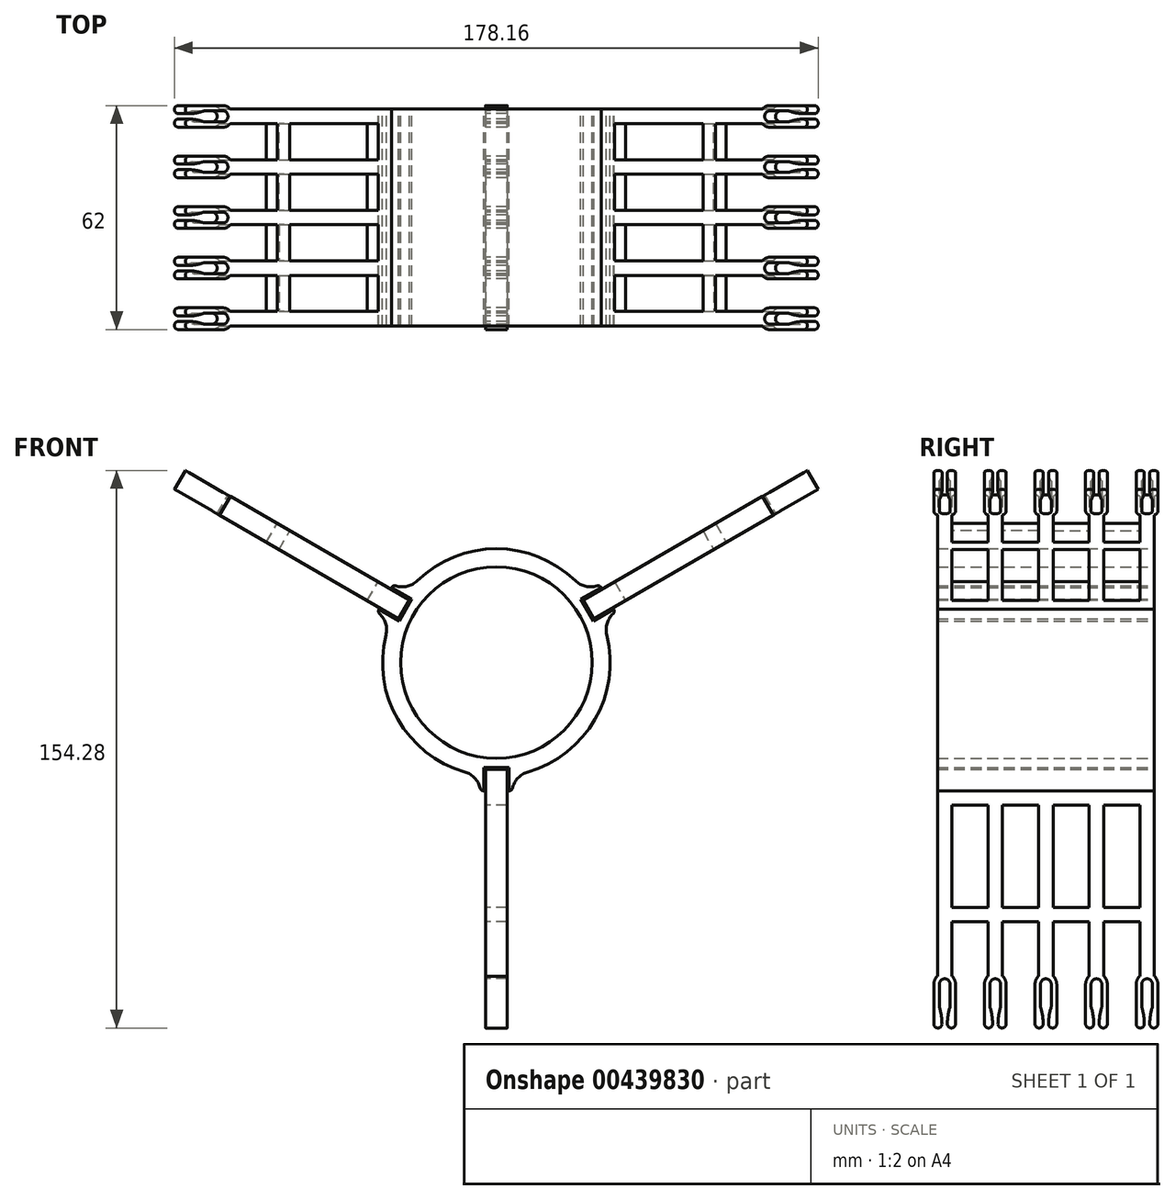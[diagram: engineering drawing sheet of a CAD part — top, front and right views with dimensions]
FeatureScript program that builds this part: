
annotation { "Feature Type Name" : "Feature", "Feature Type Description" : "" }
export const myFeature = defineFeature(function(context is Context, id is Id, definition is map)
    precondition{}
    {
        {
            var Q0;
            Q0=qCreatedBy(makeId("Right.planeOp"),FACE);
            var sketch = newSketch(context, id + "F0", { "sketchPlane" : qUnion([Q0])});
            skLineSegment(sketch, "E0.top", {"start": v(-60, -26.5) * mm, "end": v(0, -26.5) * mm});
            skLineSegment(sketch, "E1.top", {"start": v(-60, -29.5) * mm, "end": v(0, -29.5) * mm});
            skLineSegment(sketch, "E1.left", {"start": v(-60, 0) * mm, "end": v(-60, -29.5) * mm});
            skLineSegment(sketch, "E2", {"start": v(0, -100) * mm, "end": v(0, -29.5) * mm});
            skLineSegment(sketch, "E3", {"start": v(-14, -67.75) * mm, "end": v(-14, -39.5) * mm});
            skLineSegment(sketch, "E4", {"start": v(-14, -39.5) * mm, "end": v(-4, -39.5) * mm});
            skLineSegment(sketch, "E5", {"start": v(-4, -39.5) * mm, "end": v(-4, -67.75) * mm});
            skCircle(sketch, "E6", {"center": v(-4, -39.5) * mm, "radius": 4 * mm, "construction": true});
            skLineSegment(sketch, "E7", {"start": v(-14, -71.75) * mm, "end": v(-4, -71.75) * mm});
            skCircle(sketch, "E8", {"center": v(-4, -71.75) * mm, "radius": 4 * mm, "construction": true});
            skLineSegment(sketch, "E9", {"start": v(0, 0) * mm, "end": v(-60, 0) * mm});
            skLineSegment(sketch, "E10.trimOffspring", {"start": v(0, 0) * mm, "end": v(0, -29.5) * mm});
            skLineSegment(sketch, "E11", {"start": v(0, -32.5) * mm, "end": v(-60, -32.5) * mm, "construction": true});
            skLineSegment(sketch, "E12", {"start": v(0, -35.5) * mm, "end": v(-60, -35.5) * mm, "construction": true});
            skLineSegment(sketch, "E13", {"start": v(-18, -39.5) * mm, "end": v(-28, -39.5) * mm});
            skLineSegment(sketch, "E14", {"start": v(-28, -39.5) * mm, "end": v(-28, -67.75) * mm});
            skLineSegment(sketch, "E15", {"start": v(-18, -71.75) * mm, "end": v(-28, -71.75) * mm});
            skLineSegment(sketch, "E16.trimOffspring", {"start": v(-18, -39.5) * mm, "end": v(-18, -67.75) * mm});
            skLineSegment(sketch, "E17", {"start": v(-28, -67.75) * mm, "end": v(-18, -67.75) * mm});
            skLineSegment(sketch, "E18.MirrorCS", {"start": v(-46, -39.5) * mm, "end": v(-56, -39.5) * mm});
            skLineSegment(sketch, "E19.MirrorCS", {"start": v(-42, -39.5) * mm, "end": v(-42, -67.75) * mm});
            skLineSegment(sketch, "E20.MirrorCS", {"start": v(-46, -67.75) * mm, "end": v(-46, -39.5) * mm});
            skLineSegment(sketch, "E21.MirrorCS", {"start": v(-32, -39.5) * mm, "end": v(-32, -67.75) * mm});
            skLineSegment(sketch, "E22.MirrorCS", {"start": v(-58, -100) * mm, "end": v(-58, -29.5) * mm, "construction": true});
            skLineSegment(sketch, "E23.MirrorCS", {"start": v(-46, -71.75) * mm, "end": v(-56, -71.75) * mm});
            skLineSegment(sketch, "E24.MirrorCS", {"start": v(-56, -71.75) * mm, "end": v(-56, -86.76) * mm});
            skLineSegment(sketch, "E25.MirrorCS", {"start": v(-32, -67.75) * mm, "end": v(-42, -67.75) * mm});
            skLineSegment(sketch, "E26.MirrorCS", {"start": v(-42, -71.75) * mm, "end": v(-32, -71.75) * mm});
            skLineSegment(sketch, "E27.MirrorCS", {"start": v(-56, -39.5) * mm, "end": v(-56, -67.75) * mm});
            skLineSegment(sketch, "E28.MirrorCS", {"start": v(-42, -39.5) * mm, "end": v(-32, -39.5) * mm});
            skLineSegment(sketch, "E29.trimOffspring", {"start": v(-46, -67.75) * mm, "end": v(-56, -67.75) * mm});
            skLineSegment(sketch, "E30.trimOffspring", {"start": v(-14, -67.75) * mm, "end": v(-4, -67.75) * mm});
            skArc(sketch, "E31", {"start": v(-59.5, -95) * mm, "mid": v(-59.48, -95.22) * mm, "end": v(-59.43, -95.44) * mm});
            skArc(sketch, "E32", {"start": v(-56.5, -89) * mm, "mid": v(-58, -87.5) * mm, "end": v(-59.5, -89) * mm});
            skLineSegment(sketch, "E33", {"start": v(-59.5, -89) * mm, "end": v(-59.5, -95) * mm});
            skLineSegment(sketch, "E34", {"start": v(-56.5, -95) * mm, "end": v(-56.5, -89) * mm});
            skArc(sketch, "E35", {"start": v(-56.57, -95.44) * mm, "mid": v(-57.08, -97.7) * mm, "end": v(-57.25, -100) * mm});
            skArc(sketch, "E36", {"start": v(-58.75, -100) * mm, "mid": v(-58.92, -97.7) * mm, "end": v(-59.43, -95.44) * mm});
            skLineSegment(sketch, "E37", {"start": v(-61, -89) * mm, "end": v(-61, -100) * mm});
            skLineSegment(sketch, "E38", {"start": v(-55, -89) * mm, "end": v(-55, -100) * mm});
            skLineSegment(sketch, "E39.trimOffspring", {"start": v(-60, -86.76) * mm, "end": v(-60, -29.5) * mm});
            skArc(sketch, "E40.trimOffspring", {"start": v(-55, -89) * mm, "mid": v(-55.26, -87.78) * mm, "end": v(-56, -86.76) * mm});
            skArc(sketch, "E41.trimOffspring", {"start": v(-56.57, -95.44) * mm, "mid": v(-56.52, -95.22) * mm, "end": v(-56.5, -95) * mm});
            skArc(sketch, "E42.trimOffspring", {"start": v(-60, -86.76) * mm, "mid": v(-60.74, -87.78) * mm, "end": v(-61, -89) * mm});
            skArc(sketch, "E43", {"start": v(-61, -100) * mm, "mid": v(-59.87, -101.12) * mm, "end": v(-58.75, -100) * mm});
            skArc(sketch, "E44", {"start": v(-57.25, -100) * mm, "mid": v(-56.12, -101.12) * mm, "end": v(-55, -100) * mm});
            skArc(sketch, "E45.1.0.0", {"start": v(-46, -86.76) * mm, "mid": v(-46.74, -87.78) * mm, "end": v(-47, -89) * mm});
            skLineSegment(sketch, "E45.1.0.1", {"start": v(-47, -89) * mm, "end": v(-47, -100) * mm});
            skArc(sketch, "E45.1.0.2", {"start": v(-47, -100) * mm, "mid": v(-45.87, -101.12) * mm, "end": v(-44.75, -100) * mm});
            skArc(sketch, "E45.1.0.3", {"start": v(-44.75, -100) * mm, "mid": v(-44.92, -97.7) * mm, "end": v(-45.43, -95.44) * mm});
            skArc(sketch, "E45.1.0.4", {"start": v(-45.5, -95) * mm, "mid": v(-45.48, -95.22) * mm, "end": v(-45.43, -95.44) * mm});
            skLineSegment(sketch, "E45.1.0.5", {"start": v(-45.5, -89) * mm, "end": v(-45.5, -95) * mm});
            skArc(sketch, "E45.1.0.6", {"start": v(-42.5, -89) * mm, "mid": v(-44, -87.5) * mm, "end": v(-45.5, -89) * mm});
            skLineSegment(sketch, "E45.1.0.7", {"start": v(-42.5, -95) * mm, "end": v(-42.5, -89) * mm});
            skArc(sketch, "E45.1.0.8", {"start": v(-42.57, -95.44) * mm, "mid": v(-42.52, -95.22) * mm, "end": v(-42.5, -95) * mm});
            skArc(sketch, "E45.1.0.9", {"start": v(-42.57, -95.44) * mm, "mid": v(-43.08, -97.7) * mm, "end": v(-43.25, -100) * mm});
            skLineSegment(sketch, "E45.1.0.10", {"start": v(-41, -89) * mm, "end": v(-41, -100) * mm});
            skArc(sketch, "E45.1.0.11", {"start": v(-41, -89) * mm, "mid": v(-41.26, -87.78) * mm, "end": v(-42, -86.76) * mm});
            skArc(sketch, "E45.1.0.12", {"start": v(-43.25, -100) * mm, "mid": v(-42.12, -101.12) * mm, "end": v(-41, -100) * mm});
            skArc(sketch, "E45.2.0.0", {"start": v(-32, -86.76) * mm, "mid": v(-32.74, -87.78) * mm, "end": v(-33, -89) * mm});
            skLineSegment(sketch, "E45.2.0.1", {"start": v(-33, -89) * mm, "end": v(-33, -100) * mm});
            skArc(sketch, "E45.2.0.2", {"start": v(-33, -100) * mm, "mid": v(-31.87, -101.12) * mm, "end": v(-30.75, -100) * mm});
            skArc(sketch, "E45.2.0.3", {"start": v(-30.75, -100) * mm, "mid": v(-30.92, -97.7) * mm, "end": v(-31.43, -95.44) * mm});
            skArc(sketch, "E45.2.0.4", {"start": v(-31.5, -95) * mm, "mid": v(-31.48, -95.22) * mm, "end": v(-31.43, -95.44) * mm});
            skLineSegment(sketch, "E45.2.0.5", {"start": v(-31.5, -89) * mm, "end": v(-31.5, -95) * mm});
            skArc(sketch, "E45.2.0.6", {"start": v(-28.5, -89) * mm, "mid": v(-30, -87.5) * mm, "end": v(-31.5, -89) * mm});
            skLineSegment(sketch, "E45.2.0.7", {"start": v(-28.5, -95) * mm, "end": v(-28.5, -89) * mm});
            skArc(sketch, "E45.2.0.8", {"start": v(-28.57, -95.44) * mm, "mid": v(-28.52, -95.22) * mm, "end": v(-28.5, -95) * mm});
            skArc(sketch, "E45.2.0.9", {"start": v(-28.57, -95.44) * mm, "mid": v(-29.08, -97.7) * mm, "end": v(-29.25, -100) * mm});
            skLineSegment(sketch, "E45.2.0.10", {"start": v(-27, -89) * mm, "end": v(-27, -100) * mm});
            skArc(sketch, "E45.2.0.11", {"start": v(-27, -89) * mm, "mid": v(-27.26, -87.78) * mm, "end": v(-28, -86.76) * mm});
            skArc(sketch, "E45.2.0.12", {"start": v(-29.25, -100) * mm, "mid": v(-28.12, -101.12) * mm, "end": v(-27, -100) * mm});
            skArc(sketch, "E45.3.0.0", {"start": v(-18, -86.76) * mm, "mid": v(-18.74, -87.78) * mm, "end": v(-19, -89) * mm});
            skLineSegment(sketch, "E45.3.0.1", {"start": v(-19, -89) * mm, "end": v(-19, -100) * mm});
            skArc(sketch, "E45.3.0.2", {"start": v(-19, -100) * mm, "mid": v(-17.87, -101.12) * mm, "end": v(-16.75, -100) * mm});
            skArc(sketch, "E45.3.0.3", {"start": v(-16.75, -100) * mm, "mid": v(-16.92, -97.7) * mm, "end": v(-17.43, -95.44) * mm});
            skArc(sketch, "E45.3.0.4", {"start": v(-17.5, -95) * mm, "mid": v(-17.48, -95.22) * mm, "end": v(-17.43, -95.44) * mm});
            skLineSegment(sketch, "E45.3.0.5", {"start": v(-17.5, -89) * mm, "end": v(-17.5, -95) * mm});
            skArc(sketch, "E45.3.0.6", {"start": v(-14.5, -89) * mm, "mid": v(-16, -87.5) * mm, "end": v(-17.5, -89) * mm});
            skLineSegment(sketch, "E45.3.0.7", {"start": v(-14.5, -95) * mm, "end": v(-14.5, -89) * mm});
            skArc(sketch, "E45.3.0.8", {"start": v(-14.57, -95.44) * mm, "mid": v(-14.52, -95.22) * mm, "end": v(-14.5, -95) * mm});
            skArc(sketch, "E45.3.0.9", {"start": v(-14.57, -95.44) * mm, "mid": v(-15.08, -97.7) * mm, "end": v(-15.25, -100) * mm});
            skLineSegment(sketch, "E45.3.0.10", {"start": v(-13, -89) * mm, "end": v(-13, -100) * mm});
            skArc(sketch, "E45.3.0.11", {"start": v(-13, -89) * mm, "mid": v(-13.26, -87.78) * mm, "end": v(-14, -86.76) * mm});
            skArc(sketch, "E45.3.0.12", {"start": v(-15.25, -100) * mm, "mid": v(-14.12, -101.12) * mm, "end": v(-13, -100) * mm});
            skArc(sketch, "E45.4.0.0", {"start": v(-4, -86.76) * mm, "mid": v(-4.74, -87.78) * mm, "end": v(-5, -89) * mm});
            skLineSegment(sketch, "E45.4.0.1", {"start": v(-5, -89) * mm, "end": v(-5, -100) * mm});
            skArc(sketch, "E45.4.0.2", {"start": v(-5, -100) * mm, "mid": v(-3.87, -101.12) * mm, "end": v(-2.75, -100) * mm});
            skArc(sketch, "E45.4.0.3", {"start": v(-2.75, -100) * mm, "mid": v(-2.92, -97.7) * mm, "end": v(-3.43, -95.44) * mm});
            skArc(sketch, "E45.4.0.4", {"start": v(-3.5, -95) * mm, "mid": v(-3.48, -95.22) * mm, "end": v(-3.43, -95.44) * mm});
            skLineSegment(sketch, "E45.4.0.5", {"start": v(-3.5, -89) * mm, "end": v(-3.5, -95) * mm});
            skArc(sketch, "E45.4.0.6", {"start": v(-0.5, -89) * mm, "mid": v(-2, -87.5) * mm, "end": v(-3.5, -89) * mm});
            skLineSegment(sketch, "E45.4.0.7", {"start": v(-0.5, -95) * mm, "end": v(-0.5, -89) * mm});
            skArc(sketch, "E45.4.0.8", {"start": v(-0.57, -95.44) * mm, "mid": v(-0.52, -95.22) * mm, "end": v(-0.5, -95) * mm});
            skArc(sketch, "E45.4.0.9", {"start": v(-0.57, -95.44) * mm, "mid": v(-1.08, -97.7) * mm, "end": v(-1.25, -100) * mm});
            skLineSegment(sketch, "E45.4.0.10", {"start": v(1, -89) * mm, "end": v(1, -100) * mm});
            skArc(sketch, "E45.4.0.11", {"start": v(1, -89) * mm, "mid": v(0.74, -87.78) * mm, "end": v(0, -86.76) * mm});
            skArc(sketch, "E45.4.0.12", {"start": v(-1.25, -100) * mm, "mid": v(-0.12, -101.12) * mm, "end": v(1, -100) * mm});
            skLineSegment(sketch, "E45.direction1", {"start": v(-61, -89) * mm, "end": v(-47, -89) * mm, "construction": true});
            skLineSegment(sketch, "E46", {"start": v(-46, -86.76) * mm, "end": v(-46, -71.75) * mm});
            skLineSegment(sketch, "E47", {"start": v(-42, -86.76) * mm, "end": v(-42, -71.75) * mm});
            skLineSegment(sketch, "E48", {"start": v(-32, -86.76) * mm, "end": v(-32, -71.75) * mm});
            skLineSegment(sketch, "E49", {"start": v(-28, -86.76) * mm, "end": v(-28, -71.75) * mm});
            skLineSegment(sketch, "E50", {"start": v(-18, -86.76) * mm, "end": v(-18, -71.75) * mm});
            skLineSegment(sketch, "E51", {"start": v(-14, -86.76) * mm, "end": v(-14, -71.75) * mm});
            skLineSegment(sketch, "E52", {"start": v(-4, -86.76) * mm, "end": v(-4, -71.75) * mm});
            skLineSegment(sketch, "E53", {"start": v(-56, -71.75) * mm, "end": v(-60, -71.75) * mm, "construction": true});
            skLineSegment(sketch, "E54", {"start": v(-46, -71.75) * mm, "end": v(-42, -71.75) * mm, "construction": true});
            skLineSegment(sketch, "E55", {"start": v(-32, -71.75) * mm, "end": v(-28, -71.75) * mm, "construction": true});
            skLineSegment(sketch, "E56", {"start": v(-18, -71.75) * mm, "end": v(-14, -71.75) * mm, "construction": true});
            skLineSegment(sketch, "E57", {"start": v(-4, -71.75) * mm, "end": v(0, -71.75) * mm, "construction": true});
            skLineSegment(sketch, "E58", {"start": v(-58, -100) * mm, "end": v(-58, -71.75) * mm, "construction": true});
            skSolve(sketch);
        }
        {
            var Q0;
            Q0=qCreatedBy(makeId("Front.planeOp"),FACE);
            var sketch = newSketch(context, id + "F1", { "sketchPlane" : qUnion([Q0])});
            skCircle(sketch, "E59", {"center": v(0, 0) * mm, "radius": 26.5 * mm});
            skLineSegment(sketch, "E60", {"start": v(0, 31.5) * mm, "end": v(0, -35.5) * mm, "construction": true});
            skPoint(sketch, "E61", {"position": v(0, 26.5) * mm});
            skPoint(sketch, "E62", {"position": v(0, -26.5) * mm});
            skLineSegment(sketch, "E63.bottom", {"start": v(-3.5, -29) * mm, "end": v(3.5, -29) * mm});
            skLineSegment(sketch, "E63.left", {"start": v(-3.5, -29) * mm, "end": v(-3.5, -35.5) * mm});
            skLineSegment(sketch, "E63.right", {"start": v(3.5, -29) * mm, "end": v(3.5, -35.5) * mm});
            skArc(sketch, "E64", {"start": v(-4.48, -34.72) * mm, "mid": v(-5.97, -31.93) * mm, "end": v(-8.67, -30.28) * mm});
            skArc(sketch, "E65", {"start": v(8.67, -30.28) * mm, "mid": v(5.97, -31.93) * mm, "end": v(4.48, -34.72) * mm});
            skArc(sketch, "E66", {"start": v(-4.48, -34.72) * mm, "mid": v(-4.12, -35.28) * mm, "end": v(-3.5, -35.5) * mm});
            skArc(sketch, "E67", {"start": v(3.5, -35.5) * mm, "mid": v(4.12, -35.28) * mm, "end": v(4.48, -34.72) * mm});
            skLineSegment(sketch, "E68.bottom", {"start": v(-3, -29.5) * mm, "end": v(3, -29.5) * mm, "construction": true});
            skLineSegment(sketch, "E68.left", {"start": v(-3, -29.5) * mm, "end": v(-3, -35.5) * mm, "construction": true});
            skLineSegment(sketch, "E68.right", {"start": v(3, -29.5) * mm, "end": v(3, -35.5) * mm, "construction": true});
            skCircle(sketch, "E69", {"center": v(3, -29.5) * mm, "radius": 0.5 * mm, "construction": true});
            skCircle(sketch, "E70", {"center": v(-3, -29.5) * mm, "radius": 0.5 * mm, "construction": true});
            skArc(sketch, "E71", {"start": v(8.67, -30.28) * mm, "mid": v(27.28, -15.75) * mm, "end": v(30.56, 7.63) * mm});
            skLineSegment(sketch, "E72", {"start": v(-3.5, -35.5) * mm, "end": v(3.5, -35.5) * mm, "construction": true});
            skArc(sketch, "E73.1.0", {"start": v(32.3, 13.49) * mm, "mid": v(30.63, 10.8) * mm, "end": v(30.56, 7.63) * mm});
            skArc(sketch, "E73.1.1", {"start": v(32.3, 13.49) * mm, "mid": v(32.62, 14.07) * mm, "end": v(32.5, 14.72) * mm});
            skLineSegment(sketch, "E73.1.2", {"start": v(26.86, 11.47) * mm, "end": v(32.5, 14.72) * mm});
            skLineSegment(sketch, "E73.1.3", {"start": v(26.86, 11.47) * mm, "end": v(23.36, 17.53) * mm});
            skLineSegment(sketch, "E73.1.4", {"start": v(23.36, 17.53) * mm, "end": v(29, 20.78) * mm});
            skArc(sketch, "E73.1.5", {"start": v(21.89, 22.65) * mm, "mid": v(24.67, 21.13) * mm, "end": v(27.83, 21.24) * mm});
            skArc(sketch, "E73.1.6", {"start": v(29, 20.78) * mm, "mid": v(28.5, 21.21) * mm, "end": v(27.83, 21.24) * mm});
            skArc(sketch, "E73.2.0", {"start": v(-27.83, 21.24) * mm, "mid": v(-24.67, 21.13) * mm, "end": v(-21.89, 22.65) * mm});
            skArc(sketch, "E73.2.1", {"start": v(-27.83, 21.24) * mm, "mid": v(-28.5, 21.21) * mm, "end": v(-29, 20.78) * mm});
            skLineSegment(sketch, "E73.2.2", {"start": v(-23.36, 17.53) * mm, "end": v(-29, 20.78) * mm});
            skLineSegment(sketch, "E73.2.3", {"start": v(-23.36, 17.53) * mm, "end": v(-26.86, 11.47) * mm});
            skLineSegment(sketch, "E73.2.4", {"start": v(-26.86, 11.47) * mm, "end": v(-32.5, 14.72) * mm});
            skArc(sketch, "E73.2.5", {"start": v(-30.56, 7.63) * mm, "mid": v(-30.63, 10.8) * mm, "end": v(-32.3, 13.49) * mm});
            skArc(sketch, "E73.2.6", {"start": v(-32.5, 14.72) * mm, "mid": v(-32.62, 14.07) * mm, "end": v(-32.3, 13.49) * mm});
            skArc(sketch, "E74.trimOffspring", {"start": v(-30.56, 7.63) * mm, "mid": v(-27.28, -15.75) * mm, "end": v(-8.67, -30.28) * mm});
            skArc(sketch, "E75.trimOffspring", {"start": v(21.89, 22.65) * mm, "mid": v(0, 31.5) * mm, "end": v(-21.89, 22.65) * mm});
            skSolve(sketch);
        }
        {
            var Q0;
            {var subQ0=sQuery(id+"F0.wireOp",EDGE,"E1.top");Q0=makeQuery(id+"F0.imprint","IMPRINT",FACE,{"disambiguationData":[TD([[makeQuery(id+"F0.imprint","IMPRINT",EDGE,{"derivedFrom":subQ0}),-1.0]])]});}
            extrude(context, id + "F2", {"entities" : qUnion([Q0]), "endBound" : BoundingType.SYMMETRIC, "depth" : 6 * mm, "offsetDistance" : 25 * mm});
        }
        {
            var Q0;
            Q0=makeQuery(id+"F2.opExtrude","SWEPT_BODY",BODY,{"disambiguationData":[OSD([sQuery(id+"F0.wireOp",EDGE,"E1.top"),sQuery(id+"F0.wireOp",EDGE,"E2"),sQuery(id+"F0.wireOp",EDGE,"E3"),sQuery(id+"F0.wireOp",EDGE,"E4"),sQuery(id+"F0.wireOp",EDGE,"E5"),sQuery(id+"F0.wireOp",EDGE,"E7"),sQuery(id+"F0.wireOp",EDGE,"E13"),sQuery(id+"F0.wireOp",EDGE,"E14"),sQuery(id+"F0.wireOp",EDGE,"E15"),sQuery(id+"F0.wireOp",EDGE,"E16.trimOffspring"),sQuery(id+"F0.wireOp",EDGE,"E17"),sQuery(id+"F0.wireOp",EDGE,"E18.MirrorCS"),sQuery(id+"F0.wireOp",EDGE,"E19.MirrorCS"),sQuery(id+"F0.wireOp",EDGE,"E20.MirrorCS"),sQuery(id+"F0.wireOp",EDGE,"E21.MirrorCS"),sQuery(id+"F0.wireOp",EDGE,"E23.MirrorCS"),sQuery(id+"F0.wireOp",EDGE,"E24.MirrorCS"),sQuery(id+"F0.wireOp",EDGE,"E25.MirrorCS"),sQuery(id+"F0.wireOp",EDGE,"E26.MirrorCS"),sQuery(id+"F0.wireOp",EDGE,"E27.MirrorCS"),sQuery(id+"F0.wireOp",EDGE,"E28.MirrorCS"),sQuery(id+"F0.wireOp",EDGE,"E29.trimOffspring"),sQuery(id+"F0.wireOp",EDGE,"E30.trimOffspring"),sQuery(id+"F0.wireOp",EDGE,"E31"),sQuery(id+"F0.wireOp",EDGE,"E32"),sQuery(id+"F0.wireOp",EDGE,"E33"),sQuery(id+"F0.wireOp",EDGE,"E34"),sQuery(id+"F0.wireOp",EDGE,"E35"),sQuery(id+"F0.wireOp",EDGE,"E36"),sQuery(id+"F0.wireOp",EDGE,"E37"),sQuery(id+"F0.wireOp",EDGE,"E38"),sQuery(id+"F0.wireOp",EDGE,"E39.trimOffspring"),sQuery(id+"F0.wireOp",EDGE,"E40.trimOffspring"),sQuery(id+"F0.wireOp",EDGE,"E41.trimOffspring"),sQuery(id+"F0.wireOp",EDGE,"E42.trimOffspring"),sQuery(id+"F0.wireOp",EDGE,"E43"),sQuery(id+"F0.wireOp",EDGE,"E44"),sQuery(id+"F0.wireOp",EDGE,"E45.1.0.0"),sQuery(id+"F0.wireOp",EDGE,"E45.1.0.1"),sQuery(id+"F0.wireOp",EDGE,"E45.1.0.2"),sQuery(id+"F0.wireOp",EDGE,"E45.1.0.3"),sQuery(id+"F0.wireOp",EDGE,"E45.1.0.4"),sQuery(id+"F0.wireOp",EDGE,"E45.1.0.5"),sQuery(id+"F0.wireOp",EDGE,"E45.1.0.6"),sQuery(id+"F0.wireOp",EDGE,"E45.1.0.7"),sQuery(id+"F0.wireOp",EDGE,"E45.1.0.8"),sQuery(id+"F0.wireOp",EDGE,"E45.1.0.9"),sQuery(id+"F0.wireOp",EDGE,"E45.1.0.10"),sQuery(id+"F0.wireOp",EDGE,"E45.1.0.11"),sQuery(id+"F0.wireOp",EDGE,"E45.1.0.12"),sQuery(id+"F0.wireOp",EDGE,"E45.2.0.0"),sQuery(id+"F0.wireOp",EDGE,"E45.2.0.1"),sQuery(id+"F0.wireOp",EDGE,"E45.2.0.2"),sQuery(id+"F0.wireOp",EDGE,"E45.2.0.3"),sQuery(id+"F0.wireOp",EDGE,"E45.2.0.4"),sQuery(id+"F0.wireOp",EDGE,"E45.2.0.5"),sQuery(id+"F0.wireOp",EDGE,"E45.2.0.6"),sQuery(id+"F0.wireOp",EDGE,"E45.2.0.7"),sQuery(id+"F0.wireOp",EDGE,"E45.2.0.8"),sQuery(id+"F0.wireOp",EDGE,"E45.2.0.9"),sQuery(id+"F0.wireOp",EDGE,"E45.2.0.10"),sQuery(id+"F0.wireOp",EDGE,"E45.2.0.11"),sQuery(id+"F0.wireOp",EDGE,"E45.2.0.12"),sQuery(id+"F0.wireOp",EDGE,"E45.3.0.0"),sQuery(id+"F0.wireOp",EDGE,"E45.3.0.1"),sQuery(id+"F0.wireOp",EDGE,"E45.3.0.2"),sQuery(id+"F0.wireOp",EDGE,"E45.3.0.3"),sQuery(id+"F0.wireOp",EDGE,"E45.3.0.4"),sQuery(id+"F0.wireOp",EDGE,"E45.3.0.5"),sQuery(id+"F0.wireOp",EDGE,"E45.3.0.6"),sQuery(id+"F0.wireOp",EDGE,"E45.3.0.7"),sQuery(id+"F0.wireOp",EDGE,"E45.3.0.8"),sQuery(id+"F0.wireOp",EDGE,"E45.3.0.9"),sQuery(id+"F0.wireOp",EDGE,"E45.3.0.10"),sQuery(id+"F0.wireOp",EDGE,"E45.3.0.11"),sQuery(id+"F0.wireOp",EDGE,"E45.3.0.12"),sQuery(id+"F0.wireOp",EDGE,"E45.4.0.0"),sQuery(id+"F0.wireOp",EDGE,"E45.4.0.1"),sQuery(id+"F0.wireOp",EDGE,"E45.4.0.2"),sQuery(id+"F0.wireOp",EDGE,"E45.4.0.3"),sQuery(id+"F0.wireOp",EDGE,"E45.4.0.4"),sQuery(id+"F0.wireOp",EDGE,"E45.4.0.5"),sQuery(id+"F0.wireOp",EDGE,"E45.4.0.6"),sQuery(id+"F0.wireOp",EDGE,"E45.4.0.7"),sQuery(id+"F0.wireOp",EDGE,"E45.4.0.8"),sQuery(id+"F0.wireOp",EDGE,"E45.4.0.9"),sQuery(id+"F0.wireOp",EDGE,"E45.4.0.10"),sQuery(id+"F0.wireOp",EDGE,"E45.4.0.11"),sQuery(id+"F0.wireOp",EDGE,"E45.4.0.12"),sQuery(id+"F0.wireOp",EDGE,"E46"),sQuery(id+"F0.wireOp",EDGE,"E47"),sQuery(id+"F0.wireOp",EDGE,"E48"),sQuery(id+"F0.wireOp",EDGE,"E49"),sQuery(id+"F0.wireOp",EDGE,"E50"),sQuery(id+"F0.wireOp",EDGE,"E51"),sQuery(id+"F0.wireOp",EDGE,"E52")])]});
            var Q1;
            Q1=sQuery(id+"F0.wireOp",EDGE,"E9");
            circularPattern(context, id + "F3", {"entities" : qUnion([Q0]), "axis" : qUnion([Q1]), "angle" : 360 * degree, "instanceCount" : 3, "equalSpace" : true});
        }
        {
            var Q0;
            Q0=makeQuery(id+"F1.imprint","IMPRINT",FACE,{"disambiguationData":[TD([[makeQuery(id+"F1.imprint","IMPRINT",EDGE,{"derivedFrom":sQuery(id+"F1.wireOp",EDGE,"E59")}),-1.0]])]});
            var Q1;
            Q1=makeQuery(id+"F3.opPattern","COPY",VERTEX,{"derivedFrom":makeQuery(id+"F2.opExtrude","CAP_VERTEX",VERTEX,{"disambiguationData":[OSD([sQuery(id+"F0.wireOp",EDGE,"E1.top"),sQuery(id+"F0.wireOp",EDGE,"E1.left"),sQuery(id+"F0.wireOp",EDGE,"E39.trimOffspring")])],"isStart":false}),"instanceName":"2"});
            extrude(context, id + "F4", {"entities" : qUnion([Q0]), "endBound" : BoundingType.UP_TO_VERTEX, "depth" : 25 * mm, "endBoundEntityVertex" : qUnion([Q1]), "offsetDistance" : 25 * mm});
        }
    });
